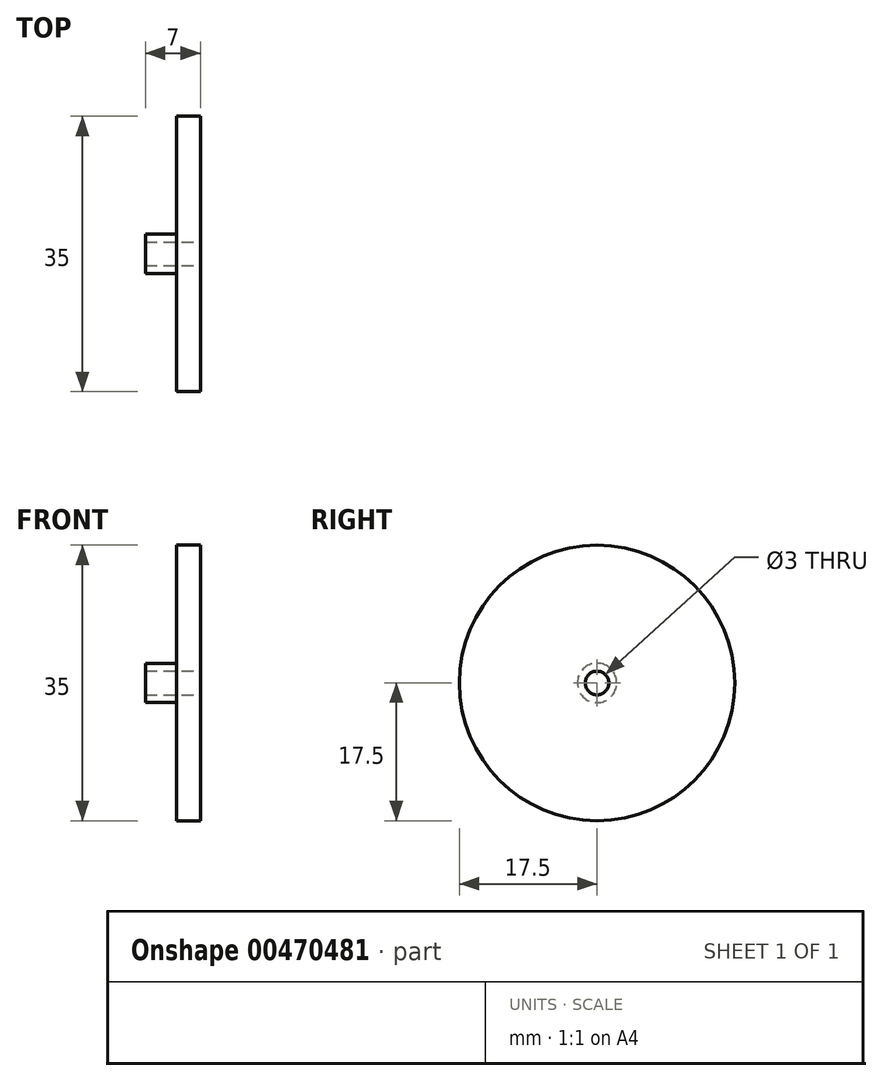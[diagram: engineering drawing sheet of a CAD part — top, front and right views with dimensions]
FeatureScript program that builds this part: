
annotation { "Feature Type Name" : "Feature", "Feature Type Description" : "" }
export const myFeature = defineFeature(function(context is Context, id is Id, definition is map)
    precondition{}
    {
        {
            var Q0;
            Q0=qCreatedBy(makeId("Right.planeOp"),FACE);
            var sketch = newSketch(context, id + "F0", { "sketchPlane" : qUnion([Q0])});
            skCircle(sketch, "E0", {"center": v(0, 0) * mm, "radius": 19.5 * mm});
            skSolve(sketch);
        }
        {
            var Q0;
            Q0=makeQuery(id+"F0.imprint","IMPRINT",FACE,{"disambiguationData":[TD([[makeQuery(id+"F0.imprint","IMPRINT",EDGE,{"derivedFrom":sQuery(id+"F0.wireOp",EDGE,"E0")}),1.0]])]});
            extrude(context, id + "F1", {"entities" : qUnion([Q0]), "endBound" : BoundingType.SYMMETRIC, "depth" : 15 * mm});
        }
        {
            var Q0;
            Q0=makeQuery(id+"F1.opExtrude","CAP_FACE",FACE,{"disambiguationData":[OSD([sQuery(id+"F0.wireOp",EDGE,"E0")])],"isStart":false});
            var sketch = newSketch(context, id + "F2", { "sketchPlane" : qUnion([Q0])});
            skCircle(sketch, "E1", {"center": v(0, 0) * mm, "radius": 17.5 * mm});
            skSolve(sketch);
        }
        {
            var Q0;
            Q0=makeQuery(id+"F1.opExtrude","CAP_FACE",FACE,{"disambiguationData":[OSD([sQuery(id+"F0.wireOp",EDGE,"E0")])],"isStart":true});
            var sketch = newSketch(context, id + "F3", { "sketchPlane" : qUnion([Q0])});
            skCircle(sketch, "E2", {"center": v(0, 0) * mm, "radius": 17.5 * mm});
            skSolve(sketch);
        }
        {
            var Q0;
            Q0=makeQuery(id+"F3.imprint","IMPRINT",FACE,{"disambiguationData":[TD([[makeQuery(id+"F3.imprint","IMPRINT",EDGE,{"derivedFrom":sQuery(id+"F3.wireOp",EDGE,"E2")}),1.0]])]});
            extrude(context, id + "F4", {"entities" : qUnion([Q0]), "operationType" : NewBodyOperationType.REMOVE, "oppositeDirection" : true, "depth" : 2 * mm});
        }
        {
            var Q0;
            Q0=makeQuery(id+"F2.imprint","IMPRINT",FACE,{"disambiguationData":[TD([[makeQuery(id+"F2.imprint","IMPRINT",EDGE,{"derivedFrom":sQuery(id+"F2.wireOp",EDGE,"E1")}),1.0]])]});
            extrude(context, id + "F5", {"entities" : qUnion([Q0]), "operationType" : NewBodyOperationType.REMOVE, "oppositeDirection" : true, "depth" : 2 * mm});
        }
        {
            var Q0;
            Q0=makeQuery(id+"F5.boolean.opBoolean","COPY",FACE,{"derivedFrom":makeQuery(id+"F5.opExtrude","CAP_FACE",FACE,{"disambiguationData":[OSD([sQuery(id+"F2.wireOp",EDGE,"E1")])],"isStart":false})});
            var sketch = newSketch(context, id + "F6", { "sketchPlane" : qUnion([Q0])});
            skCircle(sketch, "E3", {"center": v(0, 0) * mm, "radius": 1.5 * mm});
            skSolve(sketch);
        }
        {
            var Q0;
            Q0=makeQuery(id+"F6.imprint","IMPRINT",FACE,{"disambiguationData":[TD([[makeQuery(id+"F6.imprint","IMPRINT",EDGE,{"derivedFrom":sQuery(id+"F6.wireOp",EDGE,"E3")}),1.0]])]});
            extrude(context, id + "F7", {"entities" : qUnion([Q0]), "operationType" : NewBodyOperationType.REMOVE, "oppositeDirection" : true, "depth" : 25 * mm});
        }
        {
            var Q0;
            Q0=makeQuery(id+"F5.boolean.opBoolean","COPY",FACE,{"derivedFrom":makeQuery(id+"F5.opExtrude","CAP_FACE",FACE,{"disambiguationData":[OSD([sQuery(id+"F2.wireOp",EDGE,"E1")])],"isStart":false})});
            var sketch = newSketch(context, id + "F8", { "sketchPlane" : qUnion([Q0])});
            skCircle(sketch, "E4", {"center": v(0, 0) * mm, "radius": 2.5 * mm});
            skSolve(sketch);
        }
        {
            var Q0;
            Q0=makeQuery(id+"F8.imprint","IMPRINT",FACE,{"disambiguationData":[TD([[makeQuery(id+"F8.imprint","IMPRINT",EDGE,{"derivedFrom":sQuery(id+"F8.wireOp",EDGE,"E4")}),-1.0]])]});
            extrude(context, id + "F9", {"entities" : qUnion([Q0]), "operationType" : NewBodyOperationType.REMOVE, "oppositeDirection" : true, "depth" : 4 * mm});
        }
        {
            var Q0;
            Q0=makeQuery(id+"F4.boolean.opBoolean","COPY",FACE,{"derivedFrom":makeQuery(id+"F4.opExtrude","CAP_FACE",FACE,{"disambiguationData":[OSD([sQuery(id+"F3.wireOp",EDGE,"E2")])],"isStart":false})});
            var sketch = newSketch(context, id + "F10", { "sketchPlane" : qUnion([Q0])});
            skCircle(sketch, "E5", {"center": v(0, 0) * mm, "radius": 2.5 * mm});
            skSolve(sketch);
        }
        {
            var Q0;
            Q0=makeQuery(id+"F10.imprint","IMPRINT",FACE,{"disambiguationData":[TD([[makeQuery(id+"F10.imprint","IMPRINT",EDGE,{"derivedFrom":sQuery(id+"F10.wireOp",EDGE,"E5")}),-1.0]])]});
            extrude(context, id + "F11", {"entities" : qUnion([Q0]), "operationType" : NewBodyOperationType.REMOVE, "oppositeDirection" : true, "depth" : 4 * mm});
        }
        {
            var Q0;
            Q0=makeQuery(id+"F1.opExtrude","CAP_FACE",FACE,{"disambiguationData":[OSD([sQuery(id+"F0.wireOp",EDGE,"E0")])],"isStart":false});
            var sketch = newSketch(context, id + "F12", { "sketchPlane" : qUnion([Q0])});
            skCircle(sketch, "E6", {"center": v(0, 0) * mm, "radius": 20 * mm});
            skCircle(sketch, "E7", {"center": v(0, 0) * mm, "radius": 17.5 * mm});
            skSolve(sketch);
        }
        {
            var Q0;
            Q0=makeQuery(id+"F12.imprint","IMPRINT",FACE,{"disambiguationData":[TD([[makeQuery(id+"F12.imprint","IMPRINT",EDGE,{"derivedFrom":sQuery(id+"F12.wireOp",EDGE,"E6")}),1.0]])]});
            var Q1;
            Q1=makeQuery(id+"F12.imprint","IMPRINT",FACE,{"disambiguationData":[TD([[makeQuery(id+"F12.imprint","IMPRINT",EDGE,{"derivedFrom":sQuery(id+"F12.wireOp",EDGE,"E7")}),-1.0]])]});
            extrude(context, id + "F13", {"entities" : qUnion([Q0, Q1]), "operationType" : NewBodyOperationType.REMOVE, "oppositeDirection" : true, "depth" : 25 * mm});
        }
        {
            var Q0;
            Q0=makeQuery(id+"F5.boolean.opBoolean","COPY",FACE,{"derivedFrom":makeQuery(id+"F5.opExtrude","CAP_FACE",FACE,{"disambiguationData":[OSD([sQuery(id+"F2.wireOp",EDGE,"E1")])],"isStart":false})});
            extrude(context, id + "F14", {"entities" : qUnion([Q0]), "operationType" : NewBodyOperationType.REMOVE, "oppositeDirection" : true, "depth" : 4 * mm, "offsetDistance" : 25 * mm});
        }
    });
